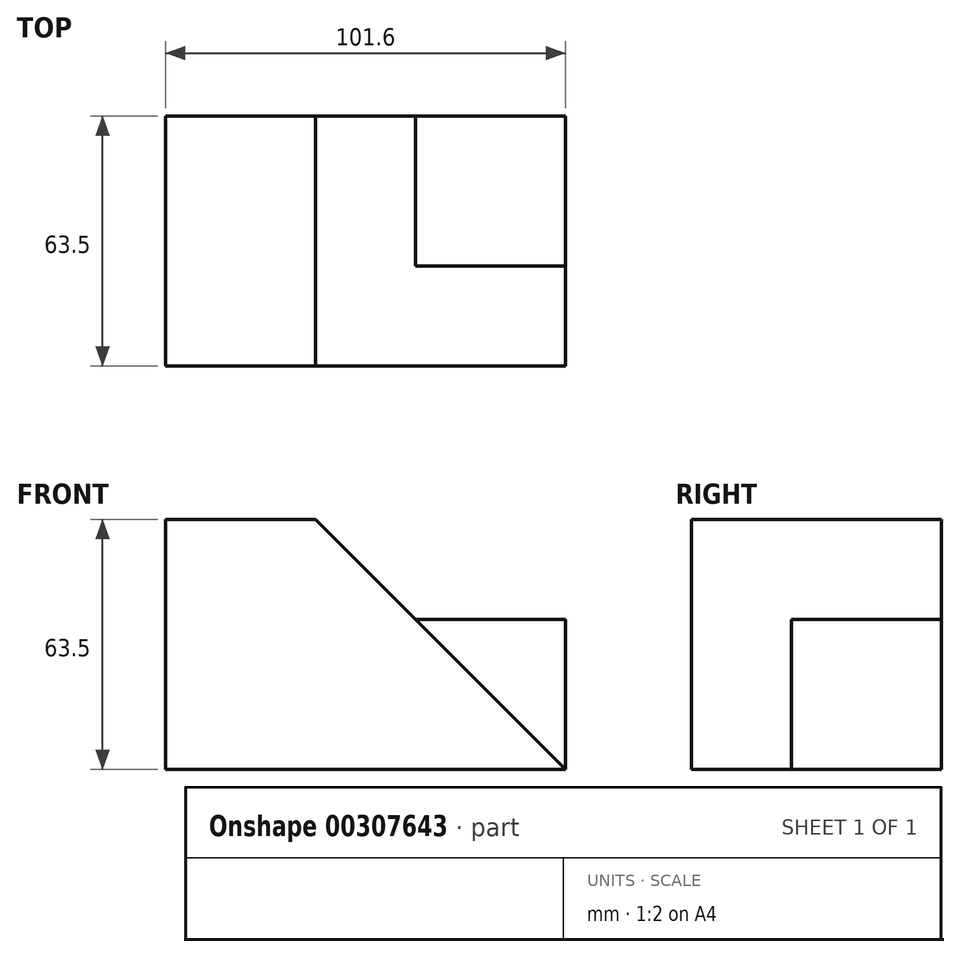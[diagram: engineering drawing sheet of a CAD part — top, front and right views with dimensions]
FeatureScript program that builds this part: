
annotation { "Feature Type Name" : "Feature", "Feature Type Description" : "" }
export const myFeature = defineFeature(function(context is Context, id is Id, definition is map)
    precondition{}
    {
        {
            var Q0;
            Q0=qCreatedBy(makeId("Front.planeOp"),FACE);
            var sketch = newSketch(context, id + "F0", { "sketchPlane" : qUnion([Q0])});
            skLineSegment(sketch, "E0", {"start": v(-32.53, -43.54) * mm, "end": v(69.07, -43.54) * mm});
            skLineSegment(sketch, "E1", {"start": v(-32.53, -43.54) * mm, "end": v(-32.53, 19.96) * mm});
            skLineSegment(sketch, "E2", {"start": v(-32.53, 19.96) * mm, "end": v(5.57, 19.96) * mm});
            skLineSegment(sketch, "E3", {"start": v(5.57, 19.96) * mm, "end": v(69.07, -43.54) * mm});
            skLineSegment(sketch, "E4", {"start": v(69.07, -43.54) * mm, "end": v(69.07, -5.44) * mm});
            skLineSegment(sketch, "E5", {"start": v(69.07, -5.44) * mm, "end": v(30.97, -5.44) * mm});
            skSolve(sketch);
        }
        {
            var Q0;
            Q0=makeQuery(id+"F0.imprint","IMPRINT",FACE,{"disambiguationData":[TD([[makeQuery(id+"F0.imprint","IMPRINT",EDGE,{"derivedFrom":sQuery(id+"F0.wireOp",EDGE,"E0")}),1.0]])]});
            extrude(context, id + "F1", {"entities" : qUnion([Q0]), "depth" : 63.5 * mm});
        }
        {
            var Q0;
            {var subQ0=sQuery(id+"F0.wireOp",EDGE,"E4");Q0=makeQuery(id+"F0.imprint","IMPRINT",FACE,{"disambiguationData":[TD([[makeQuery(id+"F0.imprint","IMPRINT",EDGE,{"derivedFrom":subQ0}),1.0]])]});}
            extrude(context, id + "F2", {"entities" : qUnion([Q0]), "depth" : 38.1 * mm});
        }
    });
